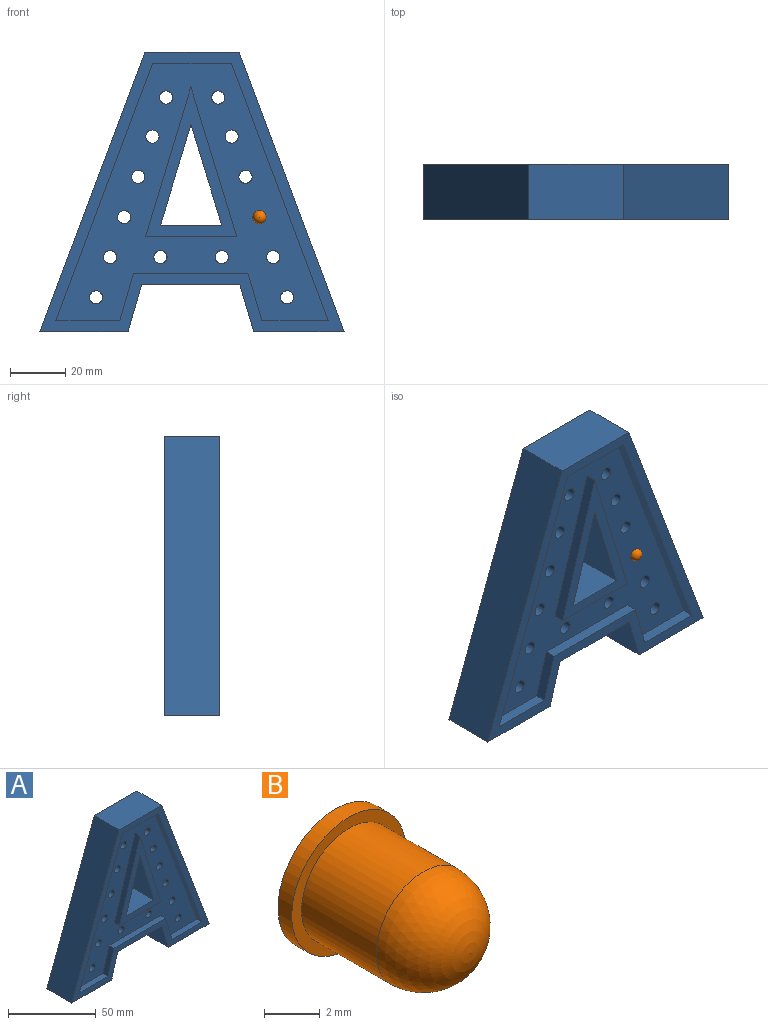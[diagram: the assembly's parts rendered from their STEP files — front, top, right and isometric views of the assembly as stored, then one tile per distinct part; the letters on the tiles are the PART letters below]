
ASSEMBLY  parts=2 mates=1
PART A: 68 faces, bbox 110.5x20x101.5 mm
  f0: cylinder r=2.4mm len=4.8mm, axis (0,-1,0), area 55.8mm2, adj f14,f44
  f1: cylinder r=2.4mm len=4.8mm, axis (0,-1,0), area 55.8mm2, adj f14,f58
  f2: cylinder r=2.4mm len=4.8mm, axis (0,-1,0), area 55.8mm2, adj f14,f46
  f3: cylinder r=2.4mm len=4.8mm, axis (0,-1,0), area 55.8mm2, adj f14,f50
  f4: cylinder r=2.4mm len=4.8mm, axis (0,-1,0), area 55.8mm2, adj f14,f64
  f5: cylinder r=2.4mm len=4.8mm, axis (0,-1,0), area 55.8mm2, adj f14,f52
  f6: cylinder r=2.4mm len=4.8mm, axis (0,-1,0), area 55.8mm2, adj f14,f62
  f7: cylinder r=2.4mm len=4.8mm, axis (0,-1,0), area 55.8mm2, adj f14,f66
  f8: cylinder r=2.4mm len=4.8mm, axis (0,-1,0), area 55.8mm2, adj f14,f48
  f9: cylinder r=2.4mm len=4.8mm, axis (0,-1,0), area 55.8mm2, adj f14,f54
  f10: cylinder r=2.4mm len=4.8mm, axis (0,-1,0), area 55.8mm2, adj f14,f42
  f11: cylinder r=2.4mm len=4.8mm, axis (0,-1,0), area 55.8mm2, adj f14,f56
  f12: cylinder r=2.4mm len=4.8mm, axis (0,-1,0), area 55.8mm2, adj f14,f40
  f13: cylinder r=2.4mm len=4.8mm, axis (0,-1,0), area 55.8mm2, adj f14,f60
  f14: plane 98.9x93.46mm, normal (0,-1,0), area 4010.6mm2, adj f0,f1,f2,f3,f4,f5,f6,f7
  f15: plane 35.59x20mm, normal (0,0,-1), area 711.9mm2, adj f16,f25,f26,f35
  f16: plane 20x17.17mm, normal (-0.96,0,-0.28), area 358.2mm2, adj f15,f17,f26,f35
  f17: plane 32.83x20mm, normal (0,0,-1), area 656.6mm2, adj f16,f18,f26,f35
  f18: plane 101.46x38.12mm, normal (0.94,0,0.35), area 2167.6mm2, adj f17,f19,f26,f35
  f19: plane 34.2x20mm, normal (0,0,1), area 683.9mm2, adj f18,f20,f26,f35
  f20: plane 101.46x38.13mm, normal (-0.94,0,0.35), area 2167.7mm2, adj f19,f21,f26,f35
  f21: plane 32.01x20mm, normal (0,0,-1), area 640.2mm2, adj f20,f25,f26,f35
  f22: plane 36.47x20mm, normal (-0.96,0,-0.29), area 763mm2, adj f23,f24,f26,f39
  f23: plane 22.28x20mm, normal (0,0,1), area 445.6mm2, adj f22,f24,f26,f39
  f24: plane 36.47x20mm, normal (0.96,0,-0.29), area 762.3mm2, adj f22,f23,f26,f39
  f25: plane 20x17.17mm, normal (0.96,0,-0.28), area 357.4mm2, adj f15,f21,f26,f35
  f26: plane 110.45x101.46mm, normal (0,1,0), area 5864.2mm2, adj f15,f16,f17,f18,f19,f20,f21,f22
  f27: plane 93.46x35.13mm, normal (0.94,0,-0.35), area 399.4mm2, adj f14,f28,f34,f35
  f28: plane 28.66x4mm, normal (0,0,-1), area 114.6mm2, adj f14,f27,f29,f35
  f29: plane 93.46x35.12mm, normal (-0.94,0,-0.35), area 399.3mm2, adj f14,f28,f30,f35
  f30: plane 24.06x4mm, normal (0,0,1), area 96.3mm2, adj f14,f29,f31,f35
  f31: plane 17.17x5.08mm, normal (0.96,0,0.28), area 71.6mm2, adj f14,f30,f32,f35
  f32: plane 41.59x4mm, normal (0,0,1), area 166.4mm2, adj f14,f31,f33,f35
  f33: plane 17.17x4.94mm, normal (-0.96,0,0.28), area 71.5mm2, adj f14,f32,f34,f35
  f34: plane 23.22x4mm, normal (0,0,1), area 92.9mm2, adj f14,f27,f33,f35
  f35: plane 110.45x101.46mm, normal (0,-1,0), area 1480.3mm2, adj f15,f16,f17,f18,f19,f20,f21,f25
  f36: plane 54.16x16.46mm, normal (-0.96,0,0.29), area 226.4mm2, adj f14,f37,f38,f39
  f37: plane 33.09x4mm, normal (0,0,-1), area 132.4mm2, adj f14,f36,f38,f39
  f38: plane 54.16x16.63mm, normal (0.96,0,0.29), area 226.6mm2, adj f14,f36,f37,f39
  f39: plane 54.16x33.09mm, normal (0,-1,0), area 489.8mm2, adj f22,f23,f24,f36,f37,f38
  f40: cone r=0mm half-angle=59deg, axis (0,1,0), area 9.7mm2, adj f12,f41
  f41: cylinder r=2.9mm len=12mm, axis (0,1,0), area 218.7mm2, adj f26,f40
  f42: cone r=0mm half-angle=59deg, axis (0,1,0), area 9.7mm2, adj f10,f43
  f43: cylinder r=2.9mm len=12mm, axis (0,1,0), area 218.7mm2, adj f26,f42
  f44: cone r=0mm half-angle=59deg, axis (0,1,0), area 9.7mm2, adj f0,f45
  f45: cylinder r=2.9mm len=12mm, axis (0,1,0), area 218.7mm2, adj f26,f44
  f46: cone r=0mm half-angle=59deg, axis (0,1,0), area 9.7mm2, adj f2,f47
  f47: cylinder r=2.9mm len=12mm, axis (0,1,0), area 218.7mm2, adj f26,f46
  f48: cone r=0mm half-angle=59deg, axis (0,1,0), area 9.7mm2, adj f8,f49
  f49: cylinder r=2.9mm len=12mm, axis (0,1,0), area 218.7mm2, adj f26,f48
  f50: cone r=0mm half-angle=59deg, axis (0,1,0), area 9.7mm2, adj f3,f51
  f51: cylinder r=2.9mm len=12mm, axis (0,1,0), area 218.7mm2, adj f26,f50
  f52: cone r=0mm half-angle=59deg, axis (0,1,0), area 9.7mm2, adj f5,f53
  f53: cylinder r=2.9mm len=12mm, axis (0,1,0), area 218.7mm2, adj f26,f52
  f54: cone r=0mm half-angle=59deg, axis (0,1,0), area 9.7mm2, adj f9,f55
  f55: cylinder r=2.9mm len=12mm, axis (0,1,0), area 218.7mm2, adj f26,f54
  f56: cone r=0mm half-angle=59deg, axis (0,1,0), area 9.7mm2, adj f11,f57
  f57: cylinder r=2.9mm len=12mm, axis (0,1,0), area 218.7mm2, adj f26,f56
  f58: cone r=0mm half-angle=59deg, axis (0,1,0), area 9.7mm2, adj f1,f59
  f59: cylinder r=2.9mm len=12mm, axis (0,1,0), area 218.7mm2, adj f26,f58
  f60: cone r=0mm half-angle=59deg, axis (0,1,0), area 9.7mm2, adj f13,f61
  f61: cylinder r=2.9mm len=12mm, axis (0,1,0), area 218.7mm2, adj f26,f60
  f62: cone r=0mm half-angle=59deg, axis (0,1,0), area 9.7mm2, adj f6,f63
  f63: cylinder r=2.9mm len=12mm, axis (0,1,0), area 218.7mm2, adj f26,f62
  f64: cone r=0mm half-angle=59deg, axis (0,1,0), area 9.7mm2, adj f4,f65
  f65: cylinder r=2.9mm len=12mm, axis (0,1,0), area 218.7mm2, adj f26,f64
  f66: cone r=0mm half-angle=59deg, axis (0,1,0), area 9.7mm2, adj f7,f67
  f67: cylinder r=2.9mm len=12mm, axis (0,1,0), area 218.7mm2, adj f26,f66
PART B: 5 faces, bbox 5.8x6.9x5.8 mm
  f0: plane 5.8x5.8mm, normal (0,-1,0), area 8.3mm2, adj f1,f4
  f1: cylinder r=2.4mm len=4.8mm, axis (0,-1,0), area 57.3mm2, adj f0,f2
  f2: sphere r=2.4mm, area 36.2mm2, adj f1
  f3: plane 5.8x5.8mm, normal (0,1,0), area 26.4mm2, adj f4
  f4: cylinder r=2.9mm len=5.8mm, axis (0,-1,0), area 12.8mm2, adj f0,f3
PLACE A at identity
PLACE B t=(-47.91,4.5,-19.64)mm
MATE fastened B.f1 <-> A.f2  axis (0,-1,0) through (-47.91,0,-9.11)mm
